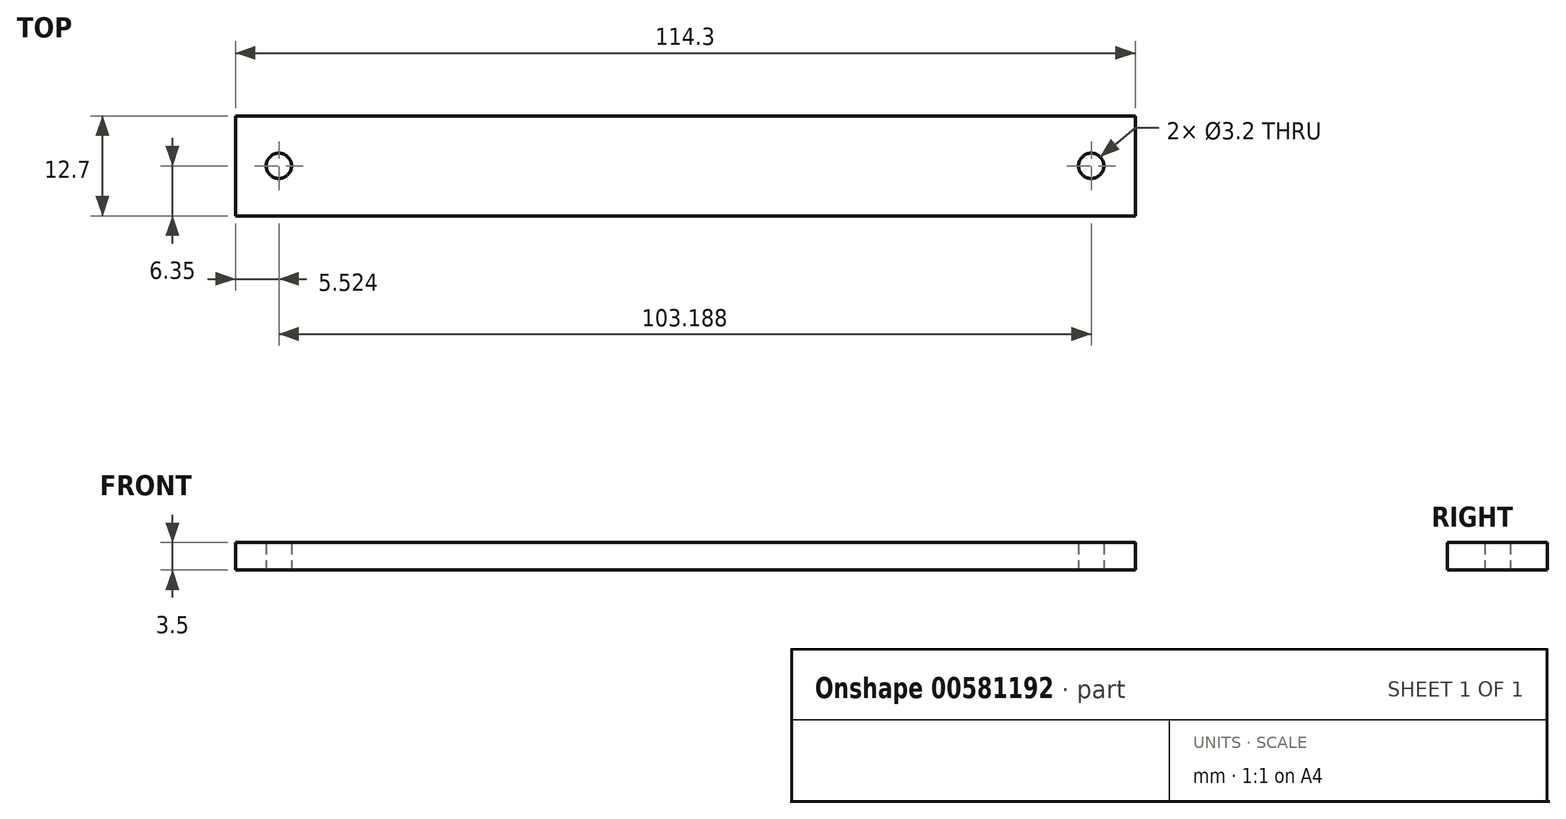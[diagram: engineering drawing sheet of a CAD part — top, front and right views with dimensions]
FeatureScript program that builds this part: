
annotation { "Feature Type Name" : "Feature", "Feature Type Description" : "" }
export const myFeature = defineFeature(function(context is Context, id is Id, definition is map)
    precondition{}
    {
        {
            var Q0;
            Q0=qCreatedBy(makeId("Top.planeOp"),FACE);
            var sketch = newSketch(context, id + "F0", { "sketchPlane" : qUnion([Q0])});
            skLineSegment(sketch, "E0.bottom", {"start": v(0, 0) * mm, "end": v(114.3, 0) * mm});
            skLineSegment(sketch, "E0.top", {"start": v(0, 12.7) * mm, "end": v(114.3, 12.7) * mm});
            skLineSegment(sketch, "E0.left", {"start": v(0, 0) * mm, "end": v(0, 12.7) * mm});
            skLineSegment(sketch, "E0.right", {"start": v(114.3, 0) * mm, "end": v(114.3, 12.7) * mm});
            skCircle(sketch, "E1", {"center": v(5.52, 6.35) * mm, "radius": 1.6 * mm});
            skCircle(sketch, "E2", {"center": v(108.71, 6.35) * mm, "radius": 1.6 * mm});
            skPoint(sketch, "E3", {"position": v(0, 6.35) * mm});
            skPoint(sketch, "E4", {"position": v(114.3, 6.35) * mm});
            skPoint(sketch, "E5", {"position": v(57.15, 12.7) * mm});
            skPoint(sketch, "E6", {"position": v(57.15, 0) * mm});
            skSolve(sketch);
        }
        {
            var Q0;
            Q0=makeQuery(id+"F0.imprint","IMPRINT",FACE,{"disambiguationData":[TD([[makeQuery(id+"F0.imprint","IMPRINT",EDGE,{"derivedFrom":sQuery(id+"F0.wireOp",EDGE,"E0.bottom")}),1.0]])]});
            extrude(context, id + "F1", {"entities" : qUnion([Q0]), "depth" : 3.5 * mm, "offsetDistance" : 25.4 * mm});
        }
    });
